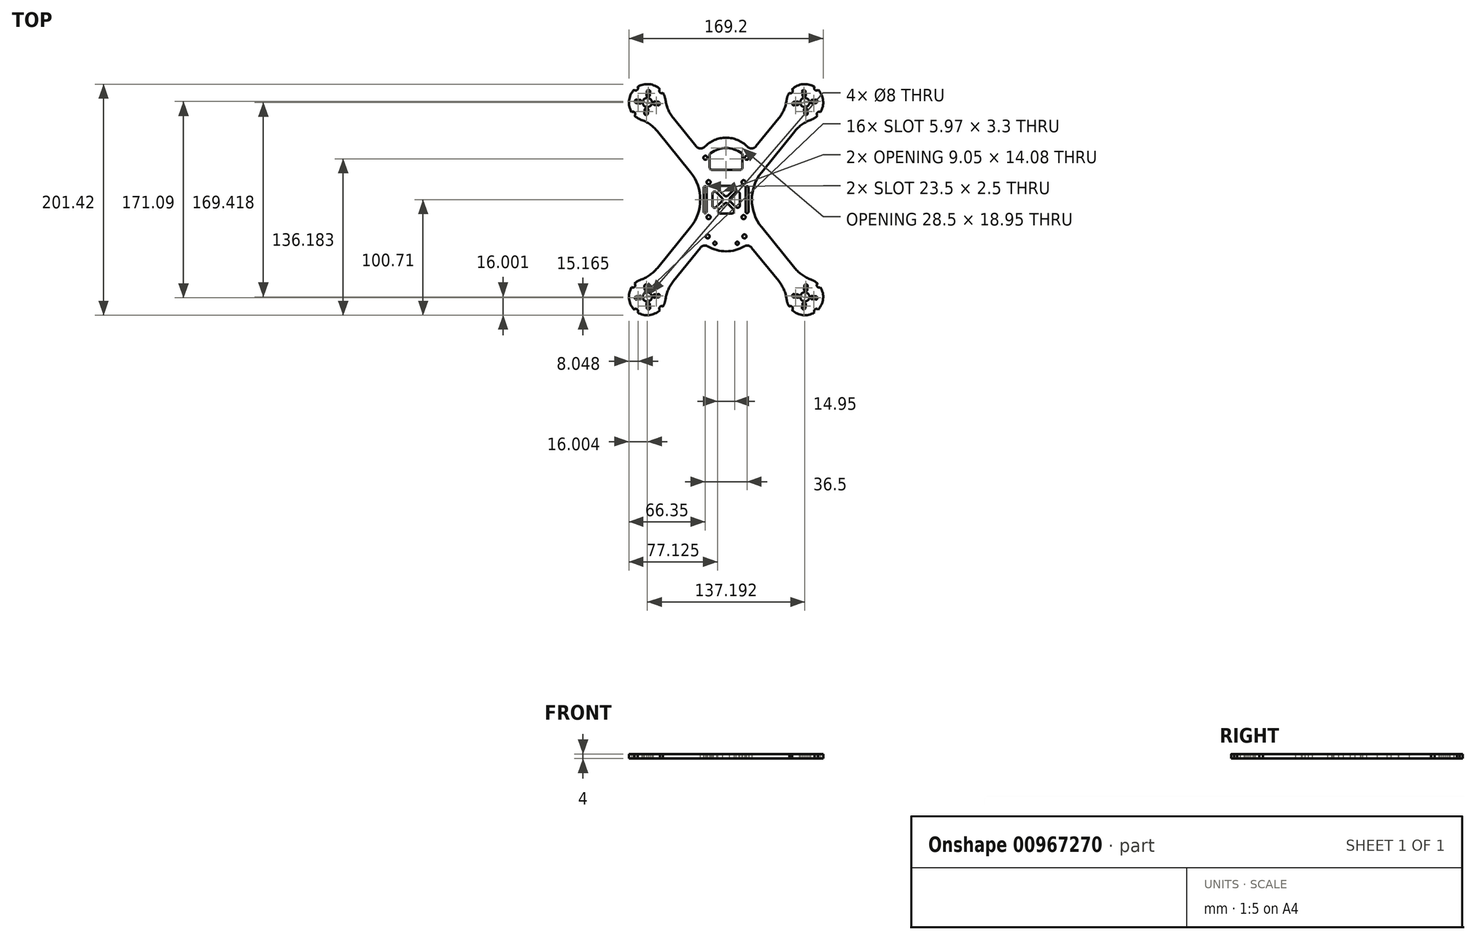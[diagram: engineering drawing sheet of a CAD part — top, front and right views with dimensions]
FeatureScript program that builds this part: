
annotation { "Feature Type Name" : "Feature", "Feature Type Description" : "" }
export const myFeature = defineFeature(function(context is Context, id is Id, definition is map)
    precondition{}
    {
        {
            var Q0;
            Q0=qCreatedBy(makeId("Top.planeOp"),FACE);
            var sketch = newSketch(context, id + "F0", { "sketchPlane" : qUnion([Q0])});
            skCircle(sketch, "E0", {"center": v(0, 0) * mm, "radius": 109 * mm, "construction": true});
            skCircle(sketch, "E1", {"center": v(68.6, 84.7) * mm, "radius": 63.5 * mm, "construction": true});
            skLineSegment(sketch, "E2", {"start": v(0, 0) * mm, "end": v(68.6, 84.7) * mm, "construction": true});
            skArc(sketch, "E3", {"start": v(73.98, 69.64) * mm, "mid": v(77.02, 71.1) * mm, "end": v(79.68, 73.17) * mm});
            skLineSegment(sketch, "E4", {"start": v(30.95, 23.91) * mm, "end": v(59.88, 59.65) * mm});
            skLineSegment(sketch, "E5", {"start": v(45.9, 70.98) * mm, "end": v(26.08, 46.5) * mm});
            skPoint(sketch, "E6.visualSharp", {"position": v(53.28, 80.1) * mm});
            skArc(sketch, "E6.filletArc", {"start": v(45.9, 70.98) * mm, "mid": v(50.4, 78.44) * mm, "end": v(52.74, 86.84) * mm});
            skPoint(sketch, "E7.visualSharp", {"position": v(67.27, 68.76) * mm});
            skArc(sketch, "E7.filletArc", {"start": v(73.98, 69.64) * mm, "mid": v(66.24, 65.61) * mm, "end": v(59.88, 59.65) * mm});
            skCircle(sketch, "E8", {"center": v(68.6, 84.7) * mm, "radius": 4 * mm});
            skLineSegment(sketch, "E9", {"start": v(0, 109) * mm, "end": v(0, 0) * mm, "construction": true});
            skLineSegment(sketch, "E10", {"start": v(0, 0) * mm, "end": v(109, 0) * mm, "construction": true});
            skArc(sketch, "E11.MirrorCS", {"start": v(-73.98, 69.64) * mm, "mid": v(-66.24, 65.61) * mm, "end": v(-59.88, 59.65) * mm});
            skArc(sketch, "E12.MirrorCS", {"start": v(-45.9, 70.98) * mm, "mid": v(-50.4, 78.44) * mm, "end": v(-52.74, 86.84) * mm});
            skPoint(sketch, "E13.MirrorP", {"position": v(-67.27, 68.76) * mm});
            skPoint(sketch, "E14.MirrorP", {"position": v(-53.28, 80.1) * mm});
            skArc(sketch, "E15.MirrorCS", {"start": v(-73.98, 69.64) * mm, "mid": v(-77.02, 71.1) * mm, "end": v(-79.68, 73.17) * mm});
            skLineSegment(sketch, "E16.MirrorCS", {"start": v(-30.95, 23.91) * mm, "end": v(-59.88, 59.65) * mm});
            skLineSegment(sketch, "E17.MirrorCS", {"start": v(-45.9, 70.98) * mm, "end": v(-26.08, 46.5) * mm});
            skCircle(sketch, "E18.MirrorC", {"center": v(-68.6, 84.7) * mm, "radius": 4 * mm});
            skCircle(sketch, "E19.MirrorC", {"center": v(-68.6, 84.7) * mm, "radius": 63.5 * mm, "construction": true});
            skLineSegment(sketch, "E20.MirrorCS", {"start": v(0, 0) * mm, "end": v(-68.6, 84.7) * mm, "construction": true});
            skArc(sketch, "E21.MirrorCS", {"start": v(-73.98, -69.64) * mm, "mid": v(-66.24, -65.61) * mm, "end": v(-59.88, -59.65) * mm});
            skArc(sketch, "E22.MirrorCS", {"start": v(-45.9, -70.98) * mm, "mid": v(-50.4, -78.44) * mm, "end": v(-52.74, -86.84) * mm});
            skPoint(sketch, "E23.MirrorP", {"position": v(-53.28, -80.1) * mm});
            skArc(sketch, "E24.MirrorCS", {"start": v(-73.98, -69.64) * mm, "mid": v(-77.02, -71.1) * mm, "end": v(-79.68, -73.17) * mm});
            skPoint(sketch, "E25.MirrorP", {"position": v(-67.27, -68.76) * mm});
            skCircle(sketch, "E26.MirrorC", {"center": v(-68.6, -84.7) * mm, "radius": 4 * mm});
            skLineSegment(sketch, "E27.MirrorCS", {"start": v(-30.95, -23.91) * mm, "end": v(-59.88, -59.65) * mm});
            skArc(sketch, "E28.MirrorCS", {"start": v(45.9, -70.98) * mm, "mid": v(50.4, -78.44) * mm, "end": v(52.74, -86.84) * mm});
            skArc(sketch, "E29.MirrorCS", {"start": v(73.98, -69.64) * mm, "mid": v(66.24, -65.61) * mm, "end": v(59.88, -59.65) * mm});
            skCircle(sketch, "E30.MirrorC", {"center": v(68.6, -84.7) * mm, "radius": 4 * mm});
            skPoint(sketch, "E31.MirrorP", {"position": v(67.27, -68.76) * mm});
            skArc(sketch, "E32.MirrorCS", {"start": v(73.98, -69.64) * mm, "mid": v(77.02, -71.1) * mm, "end": v(79.68, -73.17) * mm});
            skPoint(sketch, "E33.MirrorP", {"position": v(53.28, -80.1) * mm});
            skCircle(sketch, "E34.MirrorC", {"center": v(68.6, -84.7) * mm, "radius": 63.5 * mm, "construction": true});
            skCircle(sketch, "E35.MirrorC", {"center": v(-68.6, -84.7) * mm, "radius": 63.5 * mm, "construction": true});
            skLineSegment(sketch, "E36.MirrorCS", {"start": v(30.95, -23.91) * mm, "end": v(59.88, -59.65) * mm});
            skLineSegment(sketch, "E37.MirrorCS", {"start": v(0, 0) * mm, "end": v(-68.6, -84.7) * mm, "construction": true});
            skLineSegment(sketch, "E38.MirrorCS", {"start": v(0, 0) * mm, "end": v(68.6, -84.7) * mm, "construction": true});
            skCircle(sketch, "E39", {"center": v(-15.25, -15.25) * mm, "radius": 1.75 * mm});
            skCircle(sketch, "E40", {"center": v(15.25, -15.25) * mm, "radius": 1.75 * mm});
            skCircle(sketch, "E41.MirrorC", {"center": v(15.25, 15.25) * mm, "radius": 1.75 * mm});
            skCircle(sketch, "E42.MirrorC", {"center": v(-15.25, 15.25) * mm, "radius": 1.75 * mm});
            skLineSegment(sketch, "E43", {"start": v(-12.25, 26) * mm, "end": v(12.25, 26) * mm});
            skLineSegment(sketch, "E44", {"start": v(-14.25, 28) * mm, "end": v(-14.25, 39) * mm});
            skLineSegment(sketch, "E45", {"start": v(14.25, 28) * mm, "end": v(14.25, 39) * mm});
            skArc(sketch, "E46", {"start": v(18.61, 46.16) * mm, "mid": v(0, 54) * mm, "end": v(-18.61, 46.16) * mm});
            skPoint(sketch, "E47.visualSharp", {"position": v(-22.14, 41.64) * mm});
            skArc(sketch, "E47.filletArc", {"start": v(-26.08, 46.5) * mm, "mid": v(-22.42, 44.65) * mm, "end": v(-18.61, 46.16) * mm});
            skPoint(sketch, "E48.visualSharp", {"position": v(22.14, 41.64) * mm});
            skArc(sketch, "E48.filletArc", {"start": v(18.61, 46.16) * mm, "mid": v(22.42, 44.65) * mm, "end": v(26.08, 46.5) * mm});
            skPoint(sketch, "E49.visualSharp", {"position": v(-14.25, 26) * mm});
            skArc(sketch, "E49.filletArc", {"start": v(-14.25, 28) * mm, "mid": v(-13.66, 26.59) * mm, "end": v(-12.25, 26) * mm});
            skPoint(sketch, "E50.visualSharp", {"position": v(14.25, 26) * mm});
            skArc(sketch, "E50.filletArc", {"start": v(12.25, 26) * mm, "mid": v(13.66, 26.59) * mm, "end": v(14.25, 28) * mm});
            skPoint(sketch, "E51.visualSharp", {"position": v(-14.25, 40) * mm});
            skPoint(sketch, "E52.visualSharp", {"position": v(14.25, 44) * mm});
            skArc(sketch, "E53", {"start": v(-30.95, -23.91) * mm, "mid": v(-22.48, 0) * mm, "end": v(-30.95, 23.91) * mm});
            skArc(sketch, "E54.MirrorCS", {"start": v(30.95, -23.91) * mm, "mid": v(22.48, 0) * mm, "end": v(30.95, 23.91) * mm});
            skLineSegment(sketch, "E55", {"start": v(-45.9, -70.98) * mm, "end": v(-22.27, -41.8) * mm});
            skLineSegment(sketch, "E56", {"start": v(45.9, -70.98) * mm, "end": v(22.27, -41.8) * mm});
            skCircle(sketch, "E57", {"center": v(-16, -32) * mm, "radius": 1.75 * mm});
            skCircle(sketch, "E58.MirrorC", {"center": v(16, -32) * mm, "radius": 1.75 * mm});
            skCircle(sketch, "E59", {"center": v(-18, 36.5) * mm, "radius": 1.75 * mm});
            skCircle(sketch, "E60.MirrorC", {"center": v(18, 36.5) * mm, "radius": 1.75 * mm});
            skLineSegment(sketch, "E61.bottom", {"start": v(-19.5, 10.5) * mm, "end": v(-17, 10.5) * mm, "construction": true});
            skLineSegment(sketch, "E61.top", {"start": v(-19.5, -10.5) * mm, "end": v(-17, -10.5) * mm, "construction": true});
            skLineSegment(sketch, "E61.left", {"start": v(-19.5, 10.5) * mm, "end": v(-19.5, -10.5) * mm});
            skLineSegment(sketch, "E61.right", {"start": v(-17, 10.5) * mm, "end": v(-17, -10.5) * mm});
            skArc(sketch, "E62", {"start": v(-17, 10.5) * mm, "mid": v(-18.25, 11.75) * mm, "end": v(-19.5, 10.5) * mm});
            skArc(sketch, "E63", {"start": v(-19.5, -10.5) * mm, "mid": v(-18.25, -11.75) * mm, "end": v(-17, -10.5) * mm});
            skArc(sketch, "E64.MirrorCS", {"start": v(19.5, -10.5) * mm, "mid": v(18.25, -11.75) * mm, "end": v(17, -10.5) * mm});
            skLineSegment(sketch, "E65.MirrorCS", {"start": v(19.5, 10.5) * mm, "end": v(17, 10.5) * mm, "construction": true});
            skLineSegment(sketch, "E66.MirrorCS", {"start": v(19.5, -10.5) * mm, "end": v(17, -10.5) * mm, "construction": true});
            skLineSegment(sketch, "E67.MirrorCS", {"start": v(19.5, 10.5) * mm, "end": v(19.5, -10.5) * mm});
            skLineSegment(sketch, "E68.MirrorCS", {"start": v(17, 10.5) * mm, "end": v(17, -10.5) * mm});
            skArc(sketch, "E69.MirrorCS", {"start": v(17, 10.5) * mm, "mid": v(18.25, 11.75) * mm, "end": v(19.5, 10.5) * mm});
            skArc(sketch, "E70", {"start": v(-77.04, -98.3) * mm, "mid": v(-77.4, -95.59) * mm, "end": v(-80.14, -95.79) * mm});
            skArc(sketch, "E71", {"start": v(-82.19, -76.27) * mm, "mid": v(-79.48, -75.9) * mm, "end": v(-79.68, -73.17) * mm});
            skArc(sketch, "E72", {"start": v(-55, -93.15) * mm, "mid": v(-57.72, -93.52) * mm, "end": v(-57.51, -96.25) * mm});
            skLineSegment(sketch, "E73", {"start": v(-81.03, -74.64) * mm, "end": v(-56.16, -94.78) * mm, "construction": true});
            skArc(sketch, "E74.MirrorC", {"start": v(77.04, -98.3) * mm, "mid": v(77.4, -95.59) * mm, "end": v(80.14, -95.79) * mm});
            skArc(sketch, "E75.MirrorC", {"start": v(82.19, -76.27) * mm, "mid": v(79.48, -75.9) * mm, "end": v(79.68, -73.17) * mm});
            skArc(sketch, "E76.MirrorC", {"start": v(55, -93.15) * mm, "mid": v(57.72, -93.52) * mm, "end": v(57.51, -96.25) * mm});
            skArc(sketch, "E77.MirrorC", {"start": v(-82.19, 76.27) * mm, "mid": v(-79.48, 75.9) * mm, "end": v(-79.68, 73.17) * mm});
            skArc(sketch, "E78.MirrorC", {"start": v(-77.04, 98.3) * mm, "mid": v(-77.4, 95.59) * mm, "end": v(-80.14, 95.79) * mm});
            skArc(sketch, "E79.MirrorC", {"start": v(-55, 93.15) * mm, "mid": v(-57.72, 93.52) * mm, "end": v(-57.51, 96.25) * mm});
            skArc(sketch, "E80.MirrorC", {"start": v(82.19, 76.27) * mm, "mid": v(79.48, 75.9) * mm, "end": v(79.68, 73.17) * mm});
            skArc(sketch, "E81.MirrorC", {"start": v(77.04, 98.3) * mm, "mid": v(77.4, 95.59) * mm, "end": v(80.14, 95.79) * mm});
            skArc(sketch, "E82.MirrorC", {"start": v(55, 93.15) * mm, "mid": v(57.72, 93.52) * mm, "end": v(57.51, 96.25) * mm});
            skArc(sketch, "E83.trimOffspring", {"start": v(-77.04, 98.3) * mm, "mid": v(-66.92, 100.62) * mm, "end": v(-57.51, 96.25) * mm});
            skArc(sketch, "E84.trimOffspring", {"start": v(-82.19, 76.27) * mm, "mid": v(-84.5, 86.38) * mm, "end": v(-80.14, 95.79) * mm});
            skArc(sketch, "E85.trimOffspring", {"start": v(-55, 93.15) * mm, "mid": v(-53.54, 90.12) * mm, "end": v(-52.74, 86.84) * mm});
            skArc(sketch, "E86.trimOffspring", {"start": v(77.04, 98.3) * mm, "mid": v(66.92, 100.62) * mm, "end": v(57.51, 96.25) * mm});
            skArc(sketch, "E87.trimOffspring", {"start": v(55, 93.15) * mm, "mid": v(53.54, 90.12) * mm, "end": v(52.74, 86.84) * mm});
            skArc(sketch, "E88.trimOffspring", {"start": v(82.19, 76.27) * mm, "mid": v(84.5, 86.38) * mm, "end": v(80.14, 95.79) * mm});
            skArc(sketch, "E89.trimOffspring", {"start": v(-55.46, -93.84) * mm, "mid": v(-53.68, -90.5) * mm, "end": v(-52.74, -86.84) * mm});
            skArc(sketch, "E90.trimOffspring", {"start": v(-77.04, -98.3) * mm, "mid": v(-66.92, -100.62) * mm, "end": v(-57.51, -96.25) * mm});
            skLineSegment(sketch, "E91", {"start": v(-68.6, -84.7) * mm, "end": v(-78.67, -97.14) * mm, "construction": true});
            skArc(sketch, "E92.trimOffspring", {"start": v(-82.19, -76.27) * mm, "mid": v(-84.5, -86.38) * mm, "end": v(-80.14, -95.79) * mm});
            skArc(sketch, "E93.trimOffspring", {"start": v(82.19, -76.27) * mm, "mid": v(84.5, -86.38) * mm, "end": v(80.14, -95.79) * mm});
            skArc(sketch, "E94.trimOffspring", {"start": v(55, -93.15) * mm, "mid": v(53.54, -90.12) * mm, "end": v(52.74, -86.84) * mm});
            skArc(sketch, "E95.trimOffspring", {"start": v(77.04, -98.3) * mm, "mid": v(66.92, -100.62) * mm, "end": v(57.51, -96.25) * mm});
            skArc(sketch, "E96", {"start": v(13.42, 40.63) * mm, "mid": v(0, 44.95) * mm, "end": v(-13.42, 40.63) * mm});
            skArc(sketch, "E97.filletArc", {"start": v(-13.42, 40.63) * mm, "mid": v(-14.03, 39.92) * mm, "end": v(-14.25, 39) * mm});
            skPoint(sketch, "E98.visualSharp", {"position": v(14.25, 40) * mm});
            skArc(sketch, "E98.filletArc", {"start": v(14.25, 39) * mm, "mid": v(14.03, 39.92) * mm, "end": v(13.42, 40.63) * mm});
            skLineSegment(sketch, "E99", {"start": v(68.6, -84.7) * mm, "end": v(70.27, -68.8) * mm, "construction": true});
            skArc(sketch, "E100", {"start": v(67.78, -78.09) * mm, "mid": v(69.12, -79.74) * mm, "end": v(70.77, -78.4) * mm});
            skArc(sketch, "E101", {"start": v(71.08, -75.42) * mm, "mid": v(69.75, -73.77) * mm, "end": v(68.1, -75.1) * mm});
            skLineSegment(sketch, "E102", {"start": v(70.77, -78.4) * mm, "end": v(71.08, -75.42) * mm});
            skLineSegment(sketch, "E103", {"start": v(67.78, -78.09) * mm, "end": v(68.1, -75.1) * mm});
            skArc(sketch, "E104.1.0", {"start": v(61.97, -85.52) * mm, "mid": v(63.62, -84.19) * mm, "end": v(62.29, -82.54) * mm});
            skLineSegment(sketch, "E104.1.1", {"start": v(61.97, -85.52) * mm, "end": v(59, -85.2) * mm});
            skArc(sketch, "E104.1.2", {"start": v(59.3, -82.22) * mm, "mid": v(57.66, -83.56) * mm, "end": v(59, -85.2) * mm});
            skLineSegment(sketch, "E104.1.3", {"start": v(62.29, -82.54) * mm, "end": v(59.3, -82.22) * mm});
            skLineSegment(sketch, "E104.1.4", {"start": v(68.6, -84.7) * mm, "end": v(52.68, -83.04) * mm, "construction": true});
            skArc(sketch, "E104.2.0", {"start": v(69.4, -91.33) * mm, "mid": v(68.07, -89.68) * mm, "end": v(66.42, -91.02) * mm});
            skLineSegment(sketch, "E104.2.1", {"start": v(69.4, -91.33) * mm, "end": v(69.1, -94.31) * mm});
            skArc(sketch, "E104.2.2", {"start": v(66.11, -94) * mm, "mid": v(67.45, -95.65) * mm, "end": v(69.1, -94.31) * mm});
            skLineSegment(sketch, "E104.2.3", {"start": v(66.42, -91.02) * mm, "end": v(66.11, -94) * mm});
            skLineSegment(sketch, "E104.2.4", {"start": v(68.6, -84.7) * mm, "end": v(66.92, -100.62) * mm, "construction": true});
            skArc(sketch, "E104.3.0", {"start": v(75.22, -83.9) * mm, "mid": v(73.57, -85.23) * mm, "end": v(74.9, -86.88) * mm});
            skLineSegment(sketch, "E104.3.1", {"start": v(75.22, -83.9) * mm, "end": v(78.2, -84.21) * mm});
            skArc(sketch, "E104.3.2", {"start": v(77.89, -87.2) * mm, "mid": v(79.54, -85.86) * mm, "end": v(78.2, -84.21) * mm});
            skLineSegment(sketch, "E104.3.3", {"start": v(74.9, -86.88) * mm, "end": v(77.89, -87.2) * mm});
            skLineSegment(sketch, "E104.3.4", {"start": v(68.6, -84.7) * mm, "end": v(84.5, -86.38) * mm, "construction": true});
            skLineSegment(sketch, "E105.MirrorCS", {"start": v(-69.4, -91.33) * mm, "end": v(-69.1, -94.31) * mm});
            skArc(sketch, "E106.MirrorCS", {"start": v(-69.4, -91.33) * mm, "mid": v(-68.07, -89.68) * mm, "end": v(-66.42, -91.02) * mm});
            skLineSegment(sketch, "E107.MirrorCS", {"start": v(-66.42, -91.02) * mm, "end": v(-66.11, -94) * mm});
            skArc(sketch, "E108.MirrorCS", {"start": v(-66.11, -94) * mm, "mid": v(-67.45, -95.65) * mm, "end": v(-69.1, -94.31) * mm});
            skLineSegment(sketch, "E109.MirrorCS", {"start": v(-68.6, -84.7) * mm, "end": v(-66.92, -100.62) * mm, "construction": true});
            skLineSegment(sketch, "E110.MirrorCS", {"start": v(-68.6, -84.7) * mm, "end": v(-84.5, -86.38) * mm, "construction": true});
            skLineSegment(sketch, "E111.MirrorCS", {"start": v(-68.6, -84.7) * mm, "end": v(-52.68, -83.04) * mm, "construction": true});
            skLineSegment(sketch, "E112.MirrorCS", {"start": v(-68.6, -84.7) * mm, "end": v(-70.27, -68.8) * mm, "construction": true});
            skLineSegment(sketch, "E113.MirrorCS", {"start": v(-70.77, -78.4) * mm, "end": v(-71.08, -75.42) * mm});
            skLineSegment(sketch, "E114.MirrorCS", {"start": v(-67.78, -78.09) * mm, "end": v(-68.1, -75.1) * mm});
            skArc(sketch, "E115.MirrorCS", {"start": v(-71.08, -75.42) * mm, "mid": v(-69.75, -73.77) * mm, "end": v(-68.1, -75.1) * mm});
            skArc(sketch, "E116.MirrorCS", {"start": v(-67.78, -78.09) * mm, "mid": v(-69.12, -79.74) * mm, "end": v(-70.77, -78.4) * mm});
            skLineSegment(sketch, "E117.MirrorCS", {"start": v(-75.22, -83.9) * mm, "end": v(-78.2, -84.21) * mm});
            skArc(sketch, "E118.MirrorCS", {"start": v(-77.89, -87.2) * mm, "mid": v(-79.54, -85.86) * mm, "end": v(-78.2, -84.21) * mm});
            skLineSegment(sketch, "E119.MirrorCS", {"start": v(-74.9, -86.88) * mm, "end": v(-77.89, -87.2) * mm});
            skArc(sketch, "E120.MirrorCS", {"start": v(-75.22, -83.9) * mm, "mid": v(-73.57, -85.23) * mm, "end": v(-74.9, -86.88) * mm});
            skLineSegment(sketch, "E121.MirrorCS", {"start": v(-61.97, -85.52) * mm, "end": v(-59, -85.2) * mm});
            skArc(sketch, "E122.MirrorCS", {"start": v(-59.3, -82.22) * mm, "mid": v(-57.66, -83.56) * mm, "end": v(-59, -85.2) * mm});
            skLineSegment(sketch, "E123.MirrorCS", {"start": v(-62.29, -82.54) * mm, "end": v(-59.3, -82.22) * mm});
            skArc(sketch, "E124.MirrorCS", {"start": v(-61.97, -85.52) * mm, "mid": v(-63.62, -84.19) * mm, "end": v(-62.29, -82.54) * mm});
            skArc(sketch, "E125.MirrorCS", {"start": v(-75.22, 83.9) * mm, "mid": v(-73.57, 85.23) * mm, "end": v(-74.9, 86.88) * mm});
            skLineSegment(sketch, "E126.MirrorCS", {"start": v(-74.9, 86.88) * mm, "end": v(-77.89, 87.2) * mm});
            skArc(sketch, "E127.MirrorCS", {"start": v(-77.89, 87.2) * mm, "mid": v(-79.54, 85.86) * mm, "end": v(-78.2, 84.21) * mm});
            skLineSegment(sketch, "E128.MirrorCS", {"start": v(-75.22, 83.9) * mm, "end": v(-78.2, 84.21) * mm});
            skLineSegment(sketch, "E129.MirrorCS", {"start": v(-68.6, 84.7) * mm, "end": v(-84.5, 86.38) * mm, "construction": true});
            skLineSegment(sketch, "E130.MirrorCS", {"start": v(-68.6, 84.7) * mm, "end": v(-70.27, 68.8) * mm, "construction": true});
            skLineSegment(sketch, "E131.MirrorCS", {"start": v(-68.6, 84.7) * mm, "end": v(-52.68, 83.04) * mm, "construction": true});
            skLineSegment(sketch, "E132.MirrorCS", {"start": v(-68.6, 84.7) * mm, "end": v(-66.92, 100.62) * mm, "construction": true});
            skArc(sketch, "E133.MirrorCS", {"start": v(-67.78, 78.09) * mm, "mid": v(-69.12, 79.74) * mm, "end": v(-70.77, 78.4) * mm});
            skLineSegment(sketch, "E134.MirrorCS", {"start": v(-70.77, 78.4) * mm, "end": v(-71.08, 75.42) * mm});
            skLineSegment(sketch, "E135.MirrorCS", {"start": v(-67.78, 78.09) * mm, "end": v(-68.1, 75.1) * mm});
            skArc(sketch, "E136.MirrorCS", {"start": v(-71.08, 75.42) * mm, "mid": v(-69.75, 73.77) * mm, "end": v(-68.1, 75.1) * mm});
            skArc(sketch, "E137.MirrorCS", {"start": v(-61.97, 85.52) * mm, "mid": v(-63.62, 84.19) * mm, "end": v(-62.29, 82.54) * mm});
            skLineSegment(sketch, "E138.MirrorCS", {"start": v(-61.97, 85.52) * mm, "end": v(-59, 85.2) * mm});
            skLineSegment(sketch, "E139.MirrorCS", {"start": v(-62.29, 82.54) * mm, "end": v(-59.3, 82.22) * mm});
            skArc(sketch, "E140.MirrorCS", {"start": v(-59.3, 82.22) * mm, "mid": v(-57.66, 83.56) * mm, "end": v(-59, 85.2) * mm});
            skLineSegment(sketch, "E141.MirrorCS", {"start": v(-69.4, 91.33) * mm, "end": v(-69.1, 94.31) * mm});
            skArc(sketch, "E142.MirrorCS", {"start": v(-66.11, 94) * mm, "mid": v(-67.45, 95.65) * mm, "end": v(-69.1, 94.31) * mm});
            skLineSegment(sketch, "E143.MirrorCS", {"start": v(-66.42, 91.02) * mm, "end": v(-66.11, 94) * mm});
            skArc(sketch, "E144.MirrorCS", {"start": v(-69.4, 91.33) * mm, "mid": v(-68.07, 89.68) * mm, "end": v(-66.42, 91.02) * mm});
            skLineSegment(sketch, "E145.MirrorCS", {"start": v(66.42, 91.02) * mm, "end": v(66.11, 94) * mm});
            skArc(sketch, "E146.MirrorCS", {"start": v(66.11, 94) * mm, "mid": v(67.45, 95.65) * mm, "end": v(69.1, 94.31) * mm});
            skLineSegment(sketch, "E147.MirrorCS", {"start": v(69.4, 91.33) * mm, "end": v(69.1, 94.31) * mm});
            skArc(sketch, "E148.MirrorCS", {"start": v(69.4, 91.33) * mm, "mid": v(68.07, 89.68) * mm, "end": v(66.42, 91.02) * mm});
            skLineSegment(sketch, "E149.MirrorCS", {"start": v(75.22, 83.9) * mm, "end": v(78.2, 84.21) * mm});
            skArc(sketch, "E150.MirrorCS", {"start": v(77.89, 87.2) * mm, "mid": v(79.54, 85.86) * mm, "end": v(78.2, 84.21) * mm});
            skArc(sketch, "E151.MirrorCS", {"start": v(75.22, 83.9) * mm, "mid": v(73.57, 85.23) * mm, "end": v(74.9, 86.88) * mm});
            skLineSegment(sketch, "E152.MirrorCS", {"start": v(74.9, 86.88) * mm, "end": v(77.89, 87.2) * mm});
            skLineSegment(sketch, "E153.MirrorCS", {"start": v(70.77, 78.4) * mm, "end": v(71.08, 75.42) * mm});
            skArc(sketch, "E154.MirrorCS", {"start": v(71.08, 75.42) * mm, "mid": v(69.75, 73.77) * mm, "end": v(68.1, 75.1) * mm});
            skLineSegment(sketch, "E155.MirrorCS", {"start": v(68.6, 84.7) * mm, "end": v(70.27, 68.8) * mm, "construction": true});
            skLineSegment(sketch, "E156.MirrorCS", {"start": v(67.78, 78.09) * mm, "end": v(68.1, 75.1) * mm});
            skArc(sketch, "E157.MirrorCS", {"start": v(67.78, 78.09) * mm, "mid": v(69.12, 79.74) * mm, "end": v(70.77, 78.4) * mm});
            skArc(sketch, "E158.MirrorCS", {"start": v(59.3, 82.22) * mm, "mid": v(57.66, 83.56) * mm, "end": v(59, 85.2) * mm});
            skLineSegment(sketch, "E159.MirrorCS", {"start": v(62.29, 82.54) * mm, "end": v(59.3, 82.22) * mm});
            skLineSegment(sketch, "E160.MirrorCS", {"start": v(61.97, 85.52) * mm, "end": v(59, 85.2) * mm});
            skArc(sketch, "E161.MirrorCS", {"start": v(61.97, 85.52) * mm, "mid": v(63.62, 84.19) * mm, "end": v(62.29, 82.54) * mm});
            skLineSegment(sketch, "E162.MirrorCS", {"start": v(68.6, 84.7) * mm, "end": v(84.5, 86.38) * mm, "construction": true});
            skLineSegment(sketch, "E163.MirrorCS", {"start": v(68.6, 84.7) * mm, "end": v(66.92, 100.62) * mm, "construction": true});
            skLineSegment(sketch, "E164.MirrorCS", {"start": v(68.6, 84.7) * mm, "end": v(52.68, 83.04) * mm, "construction": true});
            skCircle(sketch, "E165", {"center": v(16, -32) * mm, "radius": 2.5 * mm, "construction": true});
            skArc(sketch, "E166.trimOffspring", {"start": v(-15.83, -40.65) * mm, "mid": v(0, -45) * mm, "end": v(15.83, -40.65) * mm});
            skPoint(sketch, "E167.visualSharp", {"position": v(-4.3, -19.62) * mm});
            skPoint(sketch, "E168.MirrorP", {"position": v(4.3, -19.62) * mm});
            skCircle(sketch, "E169", {"center": v(-9.75, -38) * mm, "radius": 1.35 * mm});
            skCircle(sketch, "E170.MirrorC", {"center": v(9.75, -38) * mm, "radius": 1.35 * mm});
            skCircle(sketch, "E171", {"center": v(9.75, -38) * mm, "radius": 2.75 * mm, "construction": true});
            skPoint(sketch, "E172.visualSharp", {"position": v(-19.36, -38.21) * mm});
            skArc(sketch, "E172.filletArc", {"start": v(-15.83, -40.65) * mm, "mid": v(-19.27, -40.03) * mm, "end": v(-22.27, -41.8) * mm});
            skPoint(sketch, "E173.visualSharp", {"position": v(19.36, -38.21) * mm});
            skArc(sketch, "E173.filletArc", {"start": v(22.27, -41.8) * mm, "mid": v(19.27, -40.03) * mm, "end": v(15.83, -40.65) * mm});
            skSolve(sketch);
        }
        {
            var Q0;
            Q0=qSketchRegion(id+"F0",true);
            var Q1;
            Q1=makeQuery(id+"F0.imprint","IMPRINT",FACE,{"disambiguationData":[TD([[makeQuery(id+"F0.imprint","IMPRINT",EDGE,{"derivedFrom":sQuery(id+"F0.wireOp",EDGE,"1dedc878-54b1-44d6-bfa4-69265974a363.sketch_text.stroke-27")}),-1.0]])]});
            var Q2;
            Q2=makeQuery(id+"F0.imprint","IMPRINT",FACE,{"disambiguationData":[TD([[makeQuery(id+"F0.imprint","IMPRINT",EDGE,{"derivedFrom":sQuery(id+"F0.wireOp",EDGE,"1dedc878-54b1-44d6-bfa4-69265974a363.sketch_text.stroke-0")}),-1.0]])]});
            extrude(context, id + "F1", {"entities" : qUnion([Q0, Q1, Q2]), "depth" : 4 * mm});
        }
        {
            var Q0;
            Q0=makeQuery(id+"F1.opExtrude","CAP_FACE",FACE,{"disambiguationData":[OSD([sQuery(id+"F0.wireOp",EDGE,"E3"),sQuery(id+"F0.wireOp",EDGE,"E4"),sQuery(id+"F0.wireOp",EDGE,"E5"),sQuery(id+"F0.wireOp",EDGE,"E6.filletArc"),sQuery(id+"F0.wireOp",EDGE,"E7.filletArc"),sQuery(id+"F0.wireOp",EDGE,"E11.MirrorCS"),sQuery(id+"F0.wireOp",EDGE,"E12.MirrorCS"),sQuery(id+"F0.wireOp",EDGE,"E15.MirrorCS"),sQuery(id+"F0.wireOp",EDGE,"E16.MirrorCS"),sQuery(id+"F0.wireOp",EDGE,"E17.MirrorCS"),sQuery(id+"F0.wireOp",EDGE,"E18.MirrorC"),sQuery(id+"F0.wireOp",EDGE,"E21.MirrorCS"),sQuery(id+"F0.wireOp",EDGE,"E22.MirrorCS"),sQuery(id+"F0.wireOp",EDGE,"E24.MirrorCS"),sQuery(id+"F0.wireOp",EDGE,"E26.MirrorC"),sQuery(id+"F0.wireOp",EDGE,"E27.MirrorCS"),sQuery(id+"F0.wireOp",EDGE,"E28.MirrorCS"),sQuery(id+"F0.wireOp",EDGE,"E29.MirrorCS"),sQuery(id+"F0.wireOp",EDGE,"E30.MirrorC"),sQuery(id+"F0.wireOp",EDGE,"E32.MirrorCS"),sQuery(id+"F0.wireOp",EDGE,"E36.MirrorCS"),sQuery(id+"F0.wireOp",EDGE,"E39"),sQuery(id+"F0.wireOp",EDGE,"E40"),sQuery(id+"F0.wireOp",EDGE,"E41.MirrorC"),sQuery(id+"F0.wireOp",EDGE,"E42.MirrorC"),sQuery(id+"F0.wireOp",EDGE,"E43"),sQuery(id+"F0.wireOp",EDGE,"E44"),sQuery(id+"F0.wireOp",EDGE,"E45"),sQuery(id+"F0.wireOp",EDGE,"E46"),sQuery(id+"F0.wireOp",EDGE,"E47.filletArc"),sQuery(id+"F0.wireOp",EDGE,"E48.filletArc"),sQuery(id+"F0.wireOp",EDGE,"E49.filletArc"),sQuery(id+"F0.wireOp",EDGE,"E50.filletArc"),sQuery(id+"F0.wireOp",EDGE,"E53"),sQuery(id+"F0.wireOp",EDGE,"E54.MirrorCS"),sQuery(id+"F0.wireOp",EDGE,"E55"),sQuery(id+"F0.wireOp",EDGE,"E56"),sQuery(id+"F0.wireOp",EDGE,"E57"),sQuery(id+"F0.wireOp",EDGE,"E58.MirrorC"),sQuery(id+"F0.wireOp",EDGE,"E59"),sQuery(id+"F0.wireOp",EDGE,"E60.MirrorC"),sQuery(id+"F0.wireOp",EDGE,"E61.left"),sQuery(id+"F0.wireOp",EDGE,"E61.right"),sQuery(id+"F0.wireOp",EDGE,"E62"),sQuery(id+"F0.wireOp",EDGE,"E63"),sQuery(id+"F0.wireOp",EDGE,"E64.MirrorCS"),sQuery(id+"F0.wireOp",EDGE,"E67.MirrorCS"),sQuery(id+"F0.wireOp",EDGE,"E68.MirrorCS"),sQuery(id+"F0.wireOp",EDGE,"E69.MirrorCS"),sQuery(id+"F0.wireOp",EDGE,"E70"),sQuery(id+"F0.wireOp",EDGE,"E71"),sQuery(id+"F0.wireOp",EDGE,"E72"),sQuery(id+"F0.wireOp",EDGE,"E74.MirrorC"),sQuery(id+"F0.wireOp",EDGE,"E75.MirrorC"),sQuery(id+"F0.wireOp",EDGE,"E76.MirrorC"),sQuery(id+"F0.wireOp",EDGE,"E77.MirrorC"),sQuery(id+"F0.wireOp",EDGE,"E78.MirrorC"),sQuery(id+"F0.wireOp",EDGE,"E79.MirrorC"),sQuery(id+"F0.wireOp",EDGE,"E80.MirrorC"),sQuery(id+"F0.wireOp",EDGE,"E81.MirrorC"),sQuery(id+"F0.wireOp",EDGE,"E82.MirrorC"),sQuery(id+"F0.wireOp",EDGE,"E83.trimOffspring"),sQuery(id+"F0.wireOp",EDGE,"E84.trimOffspring"),sQuery(id+"F0.wireOp",EDGE,"E85.trimOffspring"),sQuery(id+"F0.wireOp",EDGE,"E86.trimOffspring"),sQuery(id+"F0.wireOp",EDGE,"E87.trimOffspring"),sQuery(id+"F0.wireOp",EDGE,"E88.trimOffspring"),sQuery(id+"F0.wireOp",EDGE,"E89.trimOffspring"),sQuery(id+"F0.wireOp",EDGE,"E90.trimOffspring"),sQuery(id+"F0.wireOp",EDGE,"E92.trimOffspring"),sQuery(id+"F0.wireOp",EDGE,"E93.trimOffspring"),sQuery(id+"F0.wireOp",EDGE,"E94.trimOffspring"),sQuery(id+"F0.wireOp",EDGE,"E95.trimOffspring"),sQuery(id+"F0.wireOp",EDGE,"E96"),sQuery(id+"F0.wireOp",EDGE,"E97.filletArc"),sQuery(id+"F0.wireOp",EDGE,"E98.filletArc"),sQuery(id+"F0.wireOp",EDGE,"E100"),sQuery(id+"F0.wireOp",EDGE,"E101"),sQuery(id+"F0.wireOp",EDGE,"E102"),sQuery(id+"F0.wireOp",EDGE,"E103"),sQuery(id+"F0.wireOp",EDGE,"E104.1.0"),sQuery(id+"F0.wireOp",EDGE,"E104.1.1"),sQuery(id+"F0.wireOp",EDGE,"E104.1.2"),sQuery(id+"F0.wireOp",EDGE,"E104.1.3"),sQuery(id+"F0.wireOp",EDGE,"E104.2.0"),sQuery(id+"F0.wireOp",EDGE,"E104.2.1"),sQuery(id+"F0.wireOp",EDGE,"E104.2.2"),sQuery(id+"F0.wireOp",EDGE,"E104.2.3"),sQuery(id+"F0.wireOp",EDGE,"E104.3.0"),sQuery(id+"F0.wireOp",EDGE,"E104.3.1"),sQuery(id+"F0.wireOp",EDGE,"E104.3.2"),sQuery(id+"F0.wireOp",EDGE,"E104.3.3"),sQuery(id+"F0.wireOp",EDGE,"E105.MirrorCS"),sQuery(id+"F0.wireOp",EDGE,"E106.MirrorCS"),sQuery(id+"F0.wireOp",EDGE,"E107.MirrorCS"),sQuery(id+"F0.wireOp",EDGE,"E108.MirrorCS"),sQuery(id+"F0.wireOp",EDGE,"E113.MirrorCS"),sQuery(id+"F0.wireOp",EDGE,"E114.MirrorCS"),sQuery(id+"F0.wireOp",EDGE,"E115.MirrorCS"),sQuery(id+"F0.wireOp",EDGE,"E116.MirrorCS"),sQuery(id+"F0.wireOp",EDGE,"E117.MirrorCS"),sQuery(id+"F0.wireOp",EDGE,"E118.MirrorCS"),sQuery(id+"F0.wireOp",EDGE,"E119.MirrorCS"),sQuery(id+"F0.wireOp",EDGE,"E120.MirrorCS"),sQuery(id+"F0.wireOp",EDGE,"E121.MirrorCS"),sQuery(id+"F0.wireOp",EDGE,"E122.MirrorCS"),sQuery(id+"F0.wireOp",EDGE,"E123.MirrorCS"),sQuery(id+"F0.wireOp",EDGE,"E124.MirrorCS"),sQuery(id+"F0.wireOp",EDGE,"E125.MirrorCS"),sQuery(id+"F0.wireOp",EDGE,"E126.MirrorCS"),sQuery(id+"F0.wireOp",EDGE,"E127.MirrorCS"),sQuery(id+"F0.wireOp",EDGE,"E128.MirrorCS"),sQuery(id+"F0.wireOp",EDGE,"E133.MirrorCS"),sQuery(id+"F0.wireOp",EDGE,"E134.MirrorCS"),sQuery(id+"F0.wireOp",EDGE,"E135.MirrorCS"),sQuery(id+"F0.wireOp",EDGE,"E136.MirrorCS"),sQuery(id+"F0.wireOp",EDGE,"E137.MirrorCS"),sQuery(id+"F0.wireOp",EDGE,"E138.MirrorCS"),sQuery(id+"F0.wireOp",EDGE,"E139.MirrorCS"),sQuery(id+"F0.wireOp",EDGE,"E140.MirrorCS"),sQuery(id+"F0.wireOp",EDGE,"E141.MirrorCS"),sQuery(id+"F0.wireOp",EDGE,"E142.MirrorCS"),sQuery(id+"F0.wireOp",EDGE,"E143.MirrorCS"),sQuery(id+"F0.wireOp",EDGE,"E144.MirrorCS"),sQuery(id+"F0.wireOp",EDGE,"E145.MirrorCS"),sQuery(id+"F0.wireOp",EDGE,"E146.MirrorCS"),sQuery(id+"F0.wireOp",EDGE,"E147.MirrorCS"),sQuery(id+"F0.wireOp",EDGE,"E148.MirrorCS"),sQuery(id+"F0.wireOp",EDGE,"E149.MirrorCS"),sQuery(id+"F0.wireOp",EDGE,"E150.MirrorCS"),sQuery(id+"F0.wireOp",EDGE,"E151.MirrorCS"),sQuery(id+"F0.wireOp",EDGE,"E152.MirrorCS"),sQuery(id+"F0.wireOp",EDGE,"E153.MirrorCS"),sQuery(id+"F0.wireOp",EDGE,"E154.MirrorCS"),sQuery(id+"F0.wireOp",EDGE,"E8"),sQuery(id+"F0.wireOp",EDGE,"E156.MirrorCS"),sQuery(id+"F0.wireOp",EDGE,"E157.MirrorCS"),sQuery(id+"F0.wireOp",EDGE,"E158.MirrorCS"),sQuery(id+"F0.wireOp",EDGE,"E159.MirrorCS"),sQuery(id+"F0.wireOp",EDGE,"E160.MirrorCS"),sQuery(id+"F0.wireOp",EDGE,"E161.MirrorCS"),sQuery(id+"F0.wireOp",EDGE,"E166.trimOffspring"),sQuery(id+"F0.wireOp",EDGE,"E169"),sQuery(id+"F0.wireOp",EDGE,"E170.MirrorC"),sQuery(id+"F0.wireOp",EDGE,"E172.filletArc"),sQuery(id+"F0.wireOp",EDGE,"E173.filletArc")])],"isStart":false});
            var sketch = newSketch(context, id + "F2", { "sketchPlane" : qUnion([Q0])});
            skLineSegment(sketch, "E174.bottom", {"start": v(-5.05, 12) * mm, "end": v(5.05, 12) * mm});
            skLineSegment(sketch, "E174.top", {"start": v(-5.05, -12) * mm, "end": v(5.05, -12) * mm});
            skLineSegment(sketch, "E174.left", {"start": v(-12, 5.05) * mm, "end": v(-12, -5.05) * mm});
            skLineSegment(sketch, "E174.right", {"start": v(12, 5.05) * mm, "end": v(12, -5.05) * mm});
            skLineSegment(sketch, "E175", {"start": v(-12, 12) * mm, "end": v(12, -12) * mm, "construction": true});
            skLineSegment(sketch, "E176", {"start": v(-12, -12) * mm, "end": v(12, 12) * mm, "construction": true});
            skLineSegment(sketch, "E177", {"start": v(-8.59, 6.46) * mm, "end": v(-3.54, 1.41) * mm});
            skLineSegment(sketch, "E178", {"start": v(-6.46, 8.59) * mm, "end": v(-1.41, 3.54) * mm});
            skLineSegment(sketch, "E179.MirrorCS", {"start": v(6.46, 8.59) * mm, "end": v(1.41, 3.54) * mm});
            skLineSegment(sketch, "E180.MirrorCS", {"start": v(8.59, 6.46) * mm, "end": v(3.54, 1.41) * mm});
            skLineSegment(sketch, "E181.trimOffspring", {"start": v(-3.54, -1.41) * mm, "end": v(-8.59, -6.46) * mm});
            skLineSegment(sketch, "E182.trimOffspring", {"start": v(1.41, -3.54) * mm, "end": v(6.46, -8.59) * mm});
            skLineSegment(sketch, "E183.trimOffspring", {"start": v(-1.41, -3.54) * mm, "end": v(-6.46, -8.59) * mm});
            skLineSegment(sketch, "E184.trimOffspring", {"start": v(3.54, -1.41) * mm, "end": v(8.59, -6.46) * mm});
            skPoint(sketch, "E185.visualSharp", {"position": v(-9.88, 12) * mm});
            skArc(sketch, "E185.filletArc", {"start": v(-5.05, 12) * mm, "mid": v(-6.9, 10.77) * mm, "end": v(-6.46, 8.59) * mm});
            skPoint(sketch, "E186.visualSharp", {"position": v(9.88, 12) * mm});
            skArc(sketch, "E186.filletArc", {"start": v(6.46, 8.59) * mm, "mid": v(6.9, 10.77) * mm, "end": v(5.05, 12) * mm});
            skPoint(sketch, "E187.visualSharp", {"position": v(0, 2.12) * mm});
            skArc(sketch, "E187.filletArc", {"start": v(-1.41, 3.54) * mm, "mid": v(0, 2.95) * mm, "end": v(1.41, 3.54) * mm});
            skPoint(sketch, "E188.visualSharp", {"position": v(-2.12, 0) * mm});
            skArc(sketch, "E188.filletArc", {"start": v(-3.54, -1.41) * mm, "mid": v(-2.95, 0) * mm, "end": v(-3.54, 1.41) * mm});
            skPoint(sketch, "E189.visualSharp", {"position": v(-12, 9.88) * mm});
            skArc(sketch, "E189.filletArc", {"start": v(-8.59, 6.46) * mm, "mid": v(-10.77, 6.9) * mm, "end": v(-12, 5.05) * mm});
            skPoint(sketch, "E190.visualSharp", {"position": v(-12, -9.88) * mm});
            skArc(sketch, "E190.filletArc", {"start": v(-12, -5.05) * mm, "mid": v(-10.77, -6.9) * mm, "end": v(-8.59, -6.46) * mm});
            skPoint(sketch, "E191.visualSharp", {"position": v(-9.88, -12) * mm});
            skArc(sketch, "E191.filletArc", {"start": v(-6.46, -8.59) * mm, "mid": v(-6.9, -10.77) * mm, "end": v(-5.05, -12) * mm});
            skPoint(sketch, "E192.visualSharp", {"position": v(9.88, -12) * mm});
            skArc(sketch, "E192.filletArc", {"start": v(5.05, -12) * mm, "mid": v(6.9, -10.77) * mm, "end": v(6.46, -8.59) * mm});
            skPoint(sketch, "E193.visualSharp", {"position": v(0, -2.12) * mm});
            skArc(sketch, "E193.filletArc", {"start": v(1.41, -3.54) * mm, "mid": v(0, -2.95) * mm, "end": v(-1.41, -3.54) * mm});
            skPoint(sketch, "E194.visualSharp", {"position": v(2.12, 0) * mm});
            skArc(sketch, "E194.filletArc", {"start": v(3.54, 1.41) * mm, "mid": v(2.95, 0) * mm, "end": v(3.54, -1.41) * mm});
            skPoint(sketch, "E195.visualSharp", {"position": v(12, -9.88) * mm});
            skArc(sketch, "E195.filletArc", {"start": v(8.59, -6.46) * mm, "mid": v(10.77, -6.9) * mm, "end": v(12, -5.05) * mm});
            skPoint(sketch, "E196.visualSharp", {"position": v(12, 9.88) * mm});
            skArc(sketch, "E196.filletArc", {"start": v(12, 5.05) * mm, "mid": v(10.77, 6.9) * mm, "end": v(8.59, 6.46) * mm});
            skSolve(sketch);
        }
        {
            var Q0;
            Q0=qSketchRegion(id+"F2",true);
            extrude(context, id + "F3", {"entities" : qUnion([Q0]), "operationType" : NewBodyOperationType.REMOVE, "oppositeDirection" : true, "depth" : 25 * mm});
        }
    });
